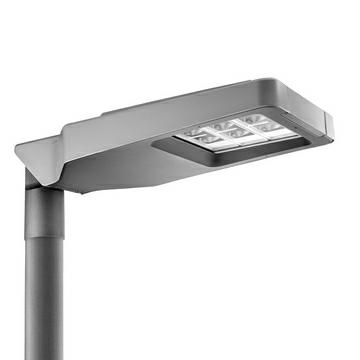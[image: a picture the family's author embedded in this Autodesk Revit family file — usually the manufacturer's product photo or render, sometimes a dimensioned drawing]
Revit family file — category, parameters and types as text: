
# Revit family: Lighting-Stradale-GEWISS-ROAD[5]MEDIUM-LED_OTTICA_WIDE_CLII
name_source: partatom
category: Apparecchi per illuminazione
units: mm (PartAtom-declared; Revit-internal decimal feet)

## family parameters
Basato su piano di lavoro = No
Condiviso = No
Punto di calcolo locali = No
Quota connettore circolare = Usa diametro
Sempre verticale = Sì
Sorgente d'illuminazione = No
Taglio con vuoti quando caricato = No
Tipo di parte = Normale

## types (1)
- Lighting-Stradale-GEWISS-ROAD[5]MEDIUM-LED_OTTICA_WIDE_CLII
    Alimentatore = Incluso
    Apparecchio a ridotta temperatura superficiale = -
    Applicazione = Esterno
    Cablaggio = Sezionatore
    Caratteristiche elettriche e gestione della luce = -
    Caratteristiche ottiche e illuminotecniche = -
    Catalogo = LIGHTING
    Catalogo Serie = ROAD [5]
    Certificazione DIN 18032-3 = -
    Certificazioni e classificazioni = -
    Classe fotobiologica = RG0
    Classe isolamento = II
    Classificazione: = -
    Codice Electrocod = 244C
    Codice digitale univoco (Datamatrix) = Attualmente non presente
    Colore = Grigio grafite
    Contesto = Illuminazione stradale e parcheggi
    Controllo abbagliamento e luminanza = G*3 - ULOR = 0
    Corpo = Alluminio pressofuso
    Corrente di pilotaggio. = 0,7A
    Descrizione = GWR5276V - ROAD5 MEDI V.WIDE 6M 4000K 0,7A CL2
    Dispositivo di protezione = DM 10KV / CM 10KV
    Distanza minima dall'oggetto illuminato = 1M
    Durata di vita = L90B10 (Tq+25°C) = 100.000 h - L90B10 (Tq+50°C) = 50.000 h
    Efficienza luminosa (lm/W) = 118
    Finitura colore = Verniciato a polveri
    Fissaggio = Testa palo - Sbraccio
    Flusso nominale (lm) = 18720
    Frequenza nominale (Hz) = 50 / 60
    Gancio di chiusura = Maniglia frontale integrata
    Garanzia = 5 anni
    Grado di protezione = IP66
    Gruppo ottico = Riflettore in PC metallizzato
    Guarnizioni = silicone antinvecchiamento
    IDF = d55d255b-eb35-4283-a5e2-ee6225d39d48
    IDT = e2497ca35bdb4cc4a5a8992b37b2b612
    IPEA = STRADALE = A++ // GRANDI AREE = A5+ // CICLOPEDONALI = A++ // AREE VERDI = A++ // CENTRO STORICO = A6+
    Immagine tipo = GWR5276M.jpg
    Inclinazione = -20° ÷ +10° sbraccio - -10° ÷ +20° testa palo
    Indice di resa cromatica = CRI-70
    Informazioni generali = -
    Installazione e manutenzione = -
    LED Life Time (L80B05) = 120000H
    Lampada = LED
    Lampada: = LED
    Lumen output (lm) = 19000
    Materiali = -
    Modello = GWR5276V
    Norma di riferimento = EN 60598-2-3, EN 60598-1 IEC/TR 62778
    Numero moduli = 6 (6x3 LED)
    Ottica = WIDE
    Peso (kg): = 9,09999999999999
    Potenza assorbita : = 161 W @ 0.7A
    Potenza di sistema = 159W
    Produttore = GEWISS S.p.A.
    Regolazione inclinazione = -20° ÷ +10° sbraccio - -10° ÷ +20° testa palo
    Resistenza agli urti = IK08
    Resistenza al filo incandescente = -
    SEO = Stradale
    Scheda Tecnica = https://www.gewiss.com
    Schermo = Vetro piano temperato spessore 4mm
    Sistema di controllo = DALI - 5 Step
    Sostituibilità gruppo ottico = Non disponibile
    Sostituibilità piastra di cablaggio = Non disponibile
    Superficie massima esposta al vento = 0,19M2
    Superficie massima esposta al vento : = 0.19 m2
    Temperatura di colore = 4000K
    Temperatura di colore: = 4000 K (CRI>70)
    Temperatura di esercizio = -25 +50 °C
    Temperatura di stoccaggio = -
    Temperatura di utilizzo = -25 +40 °C
    Tensione = 220/240 V - 50/60 Hz - Stand alone e/o Programmabile
    Tensione di alimentazione = 220 - 240 V
    Tipo di apparecchio = Apparecchiatura stradale a LED
    Tipo di installazione e montaggio = Testa palo - Sbraccio
    Tipologia = Programmabile (5 passi)
    Tipologia sorgente luminosa = LED - Non sostituibile
    Tolleranza cromatica = SDCM = 5
    URL = https://www.gewiss.com
    Vano di alimentazione = Integrato
    Versione file RFA = 20.11
    Viti esterne = Acciaio inox

## geometry (parser evidence)
native form markers: Blend x2
no freeform markers — native parametric forms only
